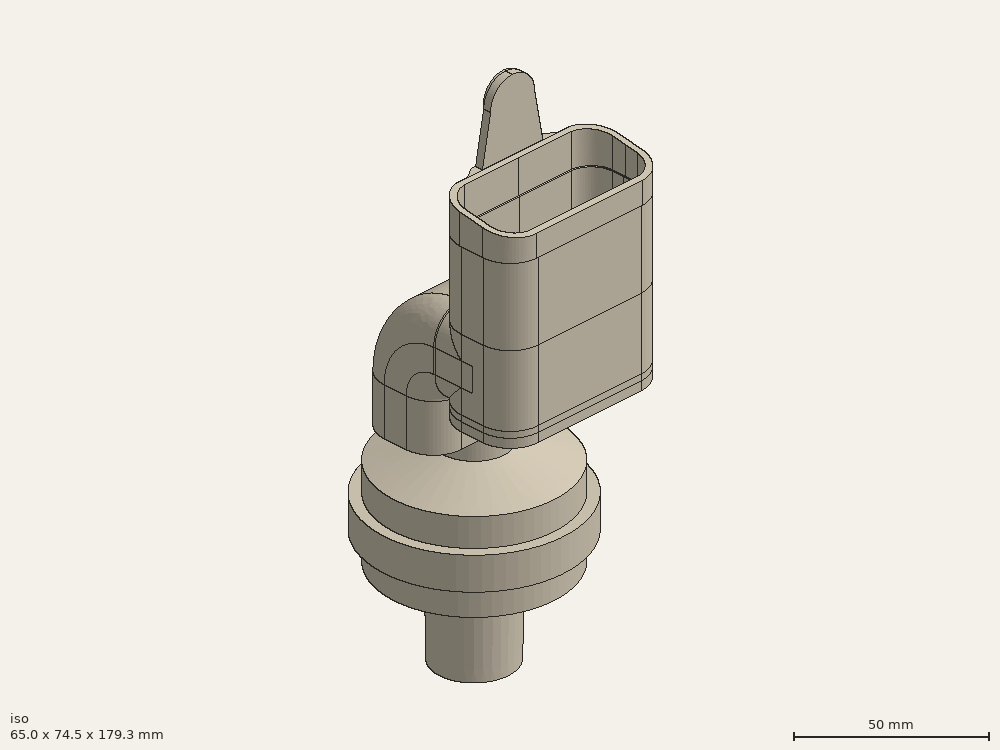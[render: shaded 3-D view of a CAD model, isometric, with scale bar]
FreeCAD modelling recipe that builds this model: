
FCSTD DOCUMENT  (FreeCAD 0.18R4 (GitTag))
Label: decathlon_easy_breath_adaptor_v2
License: All rights reserved
LicenseURL: http://en.wikipedia.org/wiki/All_rights_reserved
objects: Sketcher::SketchObject×18, PartDesign::Body×14, PartDesign::Pad×13, Part::Cut×5, Part::MultiFuse×5, PartDesign::Revolution×2, Part::Mirroring×1, Mesh::Feature×1
note: 73 computed .brp shape members not serialized (recipe doc carries the construction recipe); baked Part::Feature solids carry a one-line shape summary decoded from their .brp

FEATURE [Sketcher::SketchObject] Sketch001
  MapMode = 5
  Support = -> [XY_Plane001]
  sketch-geometry (24):
    g0: ArcOfCircle CenterX=18.75 CenterY=4 CenterZ=0 NormalX=0 NormalY=0 NormalZ=1 AngleXU=0 Radius=7.5 StartAngle=0 EndAngle=1.5708
    g1: LineSegment StartX=0 StartY=11.5 StartZ=0 EndX=18.75 EndY=11.5 EndZ=0
    g2: LineSegment StartX=26.25 StartY=4 StartZ=0 EndX=26.25 EndY=1.14244e-07 EndZ=0
    g3: LineSegment StartX=0 StartY=11.5 StartZ=0 EndX=-18.75 EndY=11.5 EndZ=0
    g4: ArcOfCircle CenterX=-18.75 CenterY=4 CenterZ=0 NormalX=0 NormalY=0 NormalZ=1 AngleXU=0 Radius=7.5 StartAngle=1.5708 EndAngle=3.14159
    g5: LineSegment StartX=-26.25 StartY=4 StartZ=0 EndX=-26.25 EndY=0 EndZ=0
    g6: LineSegment StartX=-26.25 StartY=0 StartZ=0 EndX=-26.25 EndY=-4 EndZ=0
    g7: ArcOfCircle CenterX=-18.75 CenterY=-4 CenterZ=0 NormalX=0 NormalY=0 NormalZ=1 AngleXU=0 Radius=7.5 StartAngle=3.14159 EndAngle=4.71239
    g8: ArcOfCircle CenterX=18.75 CenterY=-4 CenterZ=0 NormalX=0 NormalY=0 NormalZ=1 AngleXU=0 Radius=7.5 StartAngle=4.71239 EndAngle=6.28319
    g9: LineSegment StartX=26.25 StartY=-4 StartZ=0 EndX=26.25 EndY=1.14244e-07 EndZ=0
    g10: LineSegment StartX=-18.75 StartY=-11.5 StartZ=0 EndX=0 EndY=-11.5 EndZ=0
    g11: LineSegment StartX=0 StartY=-11.5 StartZ=0 EndX=18.75 EndY=-11.5 EndZ=0
    g12: LineSegment StartX=-18.75 StartY=-14 StartZ=0 EndX=18.75 EndY=-14 EndZ=0
    g13: ArcOfCircle CenterX=-18.75 CenterY=-4 CenterZ=0 NormalX=0 NormalY=0 NormalZ=1 AngleXU=0 Radius=10 StartAngle=3.14159 EndAngle=4.71239
    g14: LineSegment StartX=-28.75 StartY=-4 StartZ=0 EndX=-28.75 EndY=4 EndZ=0
    g15: ArcOfCircle CenterX=-18.75 CenterY=4 CenterZ=0 NormalX=0 NormalY=0 NormalZ=1 AngleXU=0 Radius=10 StartAngle=1.5708 EndAngle=3.14159
    g16: LineSegment StartX=-18.75 StartY=14 StartZ=0 EndX=-16.75 EndY=14 EndZ=0
    g17: LineSegment StartX=16.75 StartY=14 StartZ=0 EndX=18.75 EndY=14 EndZ=0
    g18: ArcOfCircle CenterX=18.75 CenterY=4 CenterZ=0 NormalX=0 NormalY=0 NormalZ=1 AngleXU=0 Radius=10 StartAngle=0 EndAngle=1.5708
    g19: ArcOfCircle CenterX=18.75 CenterY=-4 CenterZ=0 NormalX=0 NormalY=0 NormalZ=1 AngleXU=0 Radius=10 StartAngle=4.71239 EndAngle=6.28319
    g20: LineSegment StartX=28.75 StartY=4 StartZ=0 EndX=28.75 EndY=-4 EndZ=0
    g21: LineSegment StartX=-16.75 StartY=14 StartZ=0 EndX=-12.5 EndY=16.5 EndZ=0
    g22: LineSegment StartX=-12.5 StartY=16.5 StartZ=0 EndX=12.5 EndY=16.5 EndZ=0
    g23: LineSegment StartX=12.5 StartY=16.5 StartZ=0 EndX=16.75 EndY=14 EndZ=0
  constraints (71):
    c: PointOnObject(g1,g-2)
    c: Coincident(g1,g0)
    c: Horizontal(g1)
    c: Coincident(g2,g0)
    c: Vertical(g2)
    c: Coincident(g3,g1)
    c: Horizontal(g3)
    c: Coincident(g4,g3)
    c: Coincident(g5,g4)
    c: PointOnObject(g5,g-1)
    c: Vertical(g5)
    c: Coincident(g6,g5)
    c: Vertical(g6)
    c: Coincident(g7,g6)
    c: Coincident(g9,g8)
    c: Coincident(g9,g2)
    c: Vertical(g9)
    c: Coincident(g10,g7)
    c: PointOnObject(g10,g-2)
    c: Horizontal(g10)
    c: Coincident(g11,g10)
    c: Coincident(g8,g11)
    c: Equal(g3,g1)
    c: Equal(g1,g10)
    c: Equal(g10,g11)
    c: Equal(g9,g2)
    c: Equal(g2,g5)
    c: Equal(g5,g6)
    c: DistanceY(g10,g1) = 23
    c: DistanceX(g5,g2) = 52.5
    c: Symmetric(g4,g7,g-1)
    c: Symmetric(g0,g8,g-1)
    c: Symmetric(g4,g0,g-2)
    c: DistanceY(g8,g0) = 8
    c: Radius(g0) = 7.5
    c: Horizontal(g0,g0)
    c: Horizontal(g11)
    c: Horizontal(g12)
    c: Vertical(g7,g12)
    c: Coincident(g13,g7)
    c: Coincident(g13,g12)
    c: Coincident(g14,g13)
    c: Vertical(g14)
    c: Coincident(g15,g4)
    c: Coincident(g15,g14)
    c: Coincident(g16,g15)
    c: Coincident(g18,g0)
    c: Coincident(g18,g17)
    c: Vertical(g12,g8)
    c: Coincident(g19,g8)
    c: Coincident(g19,g12)
    c: Coincident(g20,g18)
    c: Coincident(g20,g19)
    c: DistanceY(g12,g7) = 2.5
    c: Horizontal(g6,g13)
    c: Horizontal(g14,g4)
    c: Vertical(g18,g19)
    c: Horizontal(g0,g18)
    c: Vertical(g17,g0)
    c: Coincident(g16,g21)
    c: Coincident(g21,g22)
    c: Coincident(g22,g23)
    c: Coincident(g23,g17)
    c: Horizontal(g16)
    c: Equal(g17,g16)
    c: Symmetric(g16,g17,g-2)
    c: DistanceY(g1,g21) = 5
    c: Symmetric(g22,g21,g-2)
    c: Horizontal(g19,g8)
    c: DistanceX(g21,g22) = 25
    c: DistanceX(g15,g16) = 2
FEATURE [Sketcher::SketchObject] Sketch002
  MapMode = 5
  Support = -> [XY_Plane002]
  sketch-geometry (26):
    g0: ArcOfCircle CenterX=18.75 CenterY=4 CenterZ=0 NormalX=0 NormalY=0 NormalZ=1 AngleXU=0 Radius=7.5 StartAngle=0 EndAngle=1.57079
    g1: LineSegment StartX=26.25 StartY=4 StartZ=0 EndX=26.25 EndY=0 EndZ=0
    g2: ArcOfCircle CenterX=-18.75 CenterY=4 CenterZ=0 NormalX=0 NormalY=0 NormalZ=1 AngleXU=0 Radius=7.5 StartAngle=1.5708 EndAngle=3.14159
    g3: LineSegment StartX=-26.25 StartY=4 StartZ=0 EndX=-26.25 EndY=0 EndZ=0
    g4: LineSegment StartX=-26.25 StartY=0 StartZ=0 EndX=-26.25 EndY=-4 EndZ=0
    g5: ArcOfCircle CenterX=-18.75 CenterY=-4 CenterZ=0 NormalX=0 NormalY=0 NormalZ=1 AngleXU=0 Radius=7.5 StartAngle=3.14159 EndAngle=4.71239
    g6: ArcOfCircle CenterX=18.75 CenterY=-4 CenterZ=0 NormalX=0 NormalY=0 NormalZ=1 AngleXU=0 Radius=7.5 StartAngle=4.71239 EndAngle=6.28319
    g7: LineSegment StartX=26.25 StartY=-4 StartZ=0 EndX=26.25 EndY=0 EndZ=0
    g8: LineSegment StartX=-18.75 StartY=-14 StartZ=0 EndX=18.75 EndY=-14 EndZ=0
    g9: ArcOfCircle CenterX=-18.75 CenterY=-4 CenterZ=0 NormalX=0 NormalY=0 NormalZ=1 AngleXU=0 Radius=10 StartAngle=3.14159 EndAngle=4.71239
    g10: LineSegment StartX=-28.75 StartY=-4 StartZ=0 EndX=-28.75 EndY=4 EndZ=0
    g11: ArcOfCircle CenterX=-18.75 CenterY=4 CenterZ=0 NormalX=0 NormalY=0 NormalZ=1 AngleXU=0 Radius=10 StartAngle=1.5708 EndAngle=3.14159
    g12: LineSegment StartX=-18.75 StartY=14 StartZ=0 EndX=18.75 EndY=14 EndZ=0
    g13: ArcOfCircle CenterX=18.75 CenterY=4 CenterZ=0 NormalX=0 NormalY=0 NormalZ=1 AngleXU=0 Radius=10 StartAngle=0 EndAngle=1.5708
    g14: ArcOfCircle CenterX=18.75 CenterY=-4 CenterZ=0 NormalX=0 NormalY=0 NormalZ=1 AngleXU=0 Radius=10 StartAngle=4.71239 EndAngle=6.28319
    g15: LineSegment StartX=28.75 StartY=4 StartZ=0 EndX=28.75 EndY=-4 EndZ=0
    g16: LineSegment StartX=-18.75 StartY=11.5 StartZ=0 EndX=-13.75 EndY=11.5 EndZ=0
    g17: LineSegment StartX=-13.75 StartY=11.5 StartZ=0 EndX=-13.75 EndY=-11.5 EndZ=0
    g18: LineSegment StartX=-13.75 StartY=-11.5 StartZ=0 EndX=-18.75 EndY=-11.5 EndZ=0
    g19: LineSegment StartX=-11.75 StartY=-11.5 StartZ=0 EndX=-11.75 EndY=11.5 EndZ=0
    g20: LineSegment StartX=-11.75 StartY=11.5 StartZ=0 EndX=11.75 EndY=11.5 EndZ=0
    g21: LineSegment StartX=11.75 StartY=11.5 StartZ=0 EndX=11.75 EndY=-11.5 EndZ=0
    g22: LineSegment StartX=11.75 StartY=-11.5 StartZ=0 EndX=-11.75 EndY=-11.5 EndZ=0
    g23: LineSegment StartX=18.75 StartY=-11.5 StartZ=0 EndX=13.75 EndY=-11.5 EndZ=0
    g24: LineSegment StartX=13.75 StartY=-11.5 StartZ=0 EndX=13.75 EndY=11.5 EndZ=0
    g25: LineSegment StartX=13.75 StartY=11.5 StartZ=0 EndX=18.75 EndY=11.5 EndZ=0
  constraints (75):
    c: Coincident(g1,g0)
    c: Vertical(g1)
    c: Coincident(g3,g2)
    c: PointOnObject(g3,g-1)
    c: Vertical(g3)
    c: Coincident(g4,g3)
    c: Vertical(g4)
    c: Coincident(g5,g4)
    c: Coincident(g7,g6)
    c: Coincident(g7,g1)
    c: Vertical(g7)
    c: Equal(g7,g1)
    c: Equal(g1,g3)
    c: Equal(g3,g4)
    c: DistanceX(g3,g1) = 52.5
    c: Symmetric(g2,g5,g-1)
    c: Symmetric(g0,g6,g-1)
    c: Symmetric(g2,g0,g-2)
    c: DistanceY(g6,g0) = 8
    c: Radius(g0) = 7.5
    c: Horizontal(g0,g0)
    c: Horizontal(g8)
    c: Vertical(g5,g8)
    c: Coincident(g9,g5)
    c: Coincident(g9,g8)
    c: Coincident(g10,g9)
    c: Vertical(g10)
    c: Coincident(g11,g2)
    c: Coincident(g11,g10)
    c: Coincident(g12,g11)
    c: Coincident(g13,g0)
    c: Vertical(g8,g6)
    c: Coincident(g14,g6)
    c: Coincident(g14,g8)
    c: Coincident(g15,g13)
    c: Coincident(g15,g14)
    c: DistanceY(g8,g5) = 2.5
    c: Horizontal(g4,g9)
    c: Horizontal(g10,g2)
    c: Vertical(g13,g14)
    c: Horizontal(g0,g13)
    c: Vertical(g13,g0)
    c: Horizontal(g12)
    c: Horizontal(g14,g6)
    c: Coincident(g16,g2)
    c: Horizontal(g16)
    c: Coincident(g16,g17)
    c: Vertical(g17)
    c: Coincident(g17,g18)
    c: Coincident(g18,g5)
    c: Vertical(g19)
    c: Coincident(g19,g20)
    c: Coincident(g20,g21)
    c: Coincident(g21,g22)
    c: Coincident(g22,g19)
    c: Tangent(g6,g23) = 1.5708
    c: Coincident(g23,g24)
    c: Vertical(g24)
    c: Coincident(g24,g25)
    c: Coincident(g25,g0)
    c: DistanceX(g19,g20) = 23.5
    c: DistanceX(g16,g19) = 2
    c: Symmetric(g24,g16,g-2)
    c: Symmetric(g20,g19,g-2)
    c: Equal(g17,g19)
    c: Equal(g19,g21)
    c: Equal(g21,g24)
    c: Horizontal(g20,g24)
    c: Coincident(g12,g13)
    c: Equal(g20,g22)
    c: Equal(g22,g20)
    c: Vertical(g2,g11)
    c: Vertical(g2,g5)
    c: Symmetric(g2,g0,g-2)
    c: Symmetric(g2,g0,g-2)
FEATURE [PartDesign::Pad] Pad002
  Length = 26
  Length2 = 100
  Profile = -> Sketch002
  Reversed = true
  Type = 0
FEATURE [PartDesign::Body] Body002
  Group = -> [Sketch002,Pad002]
  Origin = -> Origin002
  Placement = pos=(0,0,-22) rot=(0,0,1;0rad)
  Tip = -> Pad002
FEATURE [Sketcher::SketchObject] Sketch006
  MapMode = 5
  Support = -> [XY_Plane006]
  sketch-geometry (9):
    g0: LineSegment StartX=-18.75 StartY=-14 StartZ=0 EndX=18.75 EndY=-14 EndZ=0
    g1: ArcOfCircle CenterX=-18.75 CenterY=-4 CenterZ=0 NormalX=0 NormalY=0 NormalZ=1 AngleXU=0 Radius=10 StartAngle=3.14159 EndAngle=4.71239
    g2: LineSegment StartX=-28.75 StartY=-4 StartZ=0 EndX=-28.75 EndY=4 EndZ=0
    g3: ArcOfCircle CenterX=-18.75 CenterY=4 CenterZ=0 NormalX=0 NormalY=0 NormalZ=1 AngleXU=0 Radius=10 StartAngle=1.5708 EndAngle=3.14159
    g4: LineSegment StartX=-18.75 StartY=14 StartZ=0 EndX=18.75 EndY=14 EndZ=0
    g5: ArcOfCircle CenterX=18.75 CenterY=4 CenterZ=0 NormalX=0 NormalY=0 NormalZ=1 AngleXU=0 Radius=10 StartAngle=0 EndAngle=1.5708
    g6: ArcOfCircle CenterX=18.75 CenterY=-4 CenterZ=0 NormalX=0 NormalY=0 NormalZ=1 AngleXU=0 Radius=10 StartAngle=4.71239 EndAngle=6.28319
    g7: LineSegment StartX=28.75 StartY=4 StartZ=0 EndX=28.75 EndY=-4 EndZ=0
    g8: Circle CenterX=0 CenterY=0 CenterZ=0 NormalX=0 NormalY=0 NormalZ=1 AngleXU=0 Radius=11.5009
  constraints (13):
    c: Horizontal(g0)
    c: Coincident(g1,g0)
    c: Coincident(g2,g1)
    c: Vertical(g2)
    c: Coincident(g3,g2)
    c: Coincident(g4,g3)
    c: Coincident(g6,g0)
    c: Coincident(g7,g5)
    c: Coincident(g7,g6)
    c: Vertical(g5,g6)
    c: Horizontal(g4)
    c: Coincident(g4,g5)
    c: Coincident(g8,g-1)
FEATURE [PartDesign::Pad] Pad003
  Length = 16
  Length2 = 100
  Profile = -> Sketch006
  Reversed = true
  Type = 0
FEATURE [PartDesign::Body] Body006  label="lid-out"
  Group = -> [Sketch006,Pad003]
  Origin = -> Origin006
  Placement = pos=(0,28,-48) rot=(1,0,0;0rad)
  Tip = -> Pad003
FEATURE [Sketcher::SketchObject] Sketch008
  MapMode = 5
  Support = -> [XY_Plane008]
  sketch-geometry (9):
    g0: LineSegment StartX=-18.75 StartY=-14 StartZ=0 EndX=18.75 EndY=-14 EndZ=0
    g1: ArcOfCircle CenterX=-18.75 CenterY=-4 CenterZ=0 NormalX=0 NormalY=0 NormalZ=1 AngleXU=0 Radius=10 StartAngle=3.14159 EndAngle=4.71239
    g2: LineSegment StartX=-28.75 StartY=-4 StartZ=0 EndX=-28.75 EndY=4 EndZ=0
    g3: ArcOfCircle CenterX=-18.75 CenterY=4 CenterZ=0 NormalX=0 NormalY=0 NormalZ=1 AngleXU=0 Radius=10 StartAngle=1.5708 EndAngle=3.14159
    g4: LineSegment StartX=-18.75 StartY=14 StartZ=0 EndX=18.75 EndY=14 EndZ=0
    g5: ArcOfCircle CenterX=18.75 CenterY=4 CenterZ=0 NormalX=0 NormalY=0 NormalZ=1 AngleXU=0 Radius=10 StartAngle=0 EndAngle=1.5708
    g6: ArcOfCircle CenterX=18.75 CenterY=-4 CenterZ=0 NormalX=0 NormalY=0 NormalZ=1 AngleXU=0 Radius=10 StartAngle=4.71239 EndAngle=6.28319
    g7: LineSegment StartX=28.75 StartY=4 StartZ=0 EndX=28.75 EndY=-4 EndZ=0
    g8: Circle CenterX=0 CenterY=0 CenterZ=0 NormalX=0 NormalY=0 NormalZ=1 AngleXU=0 Radius=11.5009
  constraints (13):
    c: Horizontal(g0)
    c: Coincident(g1,g0)
    c: Coincident(g2,g1)
    c: Vertical(g2)
    c: Coincident(g3,g2)
    c: Coincident(g4,g3)
    c: Coincident(g6,g0)
    c: Coincident(g7,g5)
    c: Coincident(g7,g6)
    c: Vertical(g5,g6)
    c: Horizontal(g4)
    c: Coincident(g4,g5)
    c: Coincident(g8,g-1)
FEATURE [PartDesign::Pad] Pad005
  Length = 5
  Length2 = 100
  Profile = -> Sketch008
  Reversed = true
  Type = 0
FEATURE [PartDesign::Body] Body008  label="lid-in"
  Group = -> [Sketch008,Pad005]
  Origin = -> Origin008
  Placement = pos=(0,0,-46) rot=(0,0,1;0rad)
  Tip = -> Pad005
FEATURE [Sketcher::SketchObject] Sketch009
  MapMode = 5
  Support = -> [XY_Plane009]
  sketch-geometry (1):
    g0: Circle CenterX=0 CenterY=0 CenterZ=0 NormalX=0 NormalY=0 NormalZ=1 AngleXU=0 Radius=11.5
  constraints (1):
    c: Radius(g0) = 11.5
FEATURE [PartDesign::Pad] Pad006
  Length = 50
  Length2 = 100
  Profile = -> Sketch009
  Reversed = true
  Type = 0
FEATURE [Sketcher::SketchObject] Sketch010
  MapMode = 5
  Support = -> [XY_Plane010]
  sketch-geometry (12):
    g0: ArcOfCircle CenterX=18.75 CenterY=4 CenterZ=0 NormalX=0 NormalY=0 NormalZ=1 AngleXU=0 Radius=7.5 StartAngle=0 EndAngle=1.5708
    g1: LineSegment StartX=0 StartY=11.5 StartZ=0 EndX=18.75 EndY=11.5 EndZ=0
    g2: LineSegment StartX=26.25 StartY=4 StartZ=0 EndX=26.25 EndY=1.14244e-07 EndZ=0
    g3: LineSegment StartX=0 StartY=11.5 StartZ=0 EndX=-18.75 EndY=11.5 EndZ=0
    g4: ArcOfCircle CenterX=-18.75 CenterY=4 CenterZ=0 NormalX=0 NormalY=0 NormalZ=1 AngleXU=0 Radius=7.5 StartAngle=1.5708 EndAngle=3.14159
    g5: LineSegment StartX=-26.25 StartY=4 StartZ=0 EndX=-26.25 EndY=0 EndZ=0
    g6: LineSegment StartX=-26.25 StartY=0 StartZ=0 EndX=-26.25 EndY=-4 EndZ=0
    g7: ArcOfCircle CenterX=-18.75 CenterY=-4 CenterZ=0 NormalX=0 NormalY=0 NormalZ=1 AngleXU=0 Radius=7.5 StartAngle=3.14159 EndAngle=4.71239
    g8: ArcOfCircle CenterX=18.75 CenterY=-4 CenterZ=0 NormalX=0 NormalY=0 NormalZ=1 AngleXU=0 Radius=7.5 StartAngle=4.71239 EndAngle=6.28319
    g9: LineSegment StartX=26.25 StartY=-4 StartZ=0 EndX=26.25 EndY=1.14244e-07 EndZ=0
    g10: LineSegment StartX=-18.75 StartY=-11.5 StartZ=0 EndX=0 EndY=-11.5 EndZ=0
    g11: LineSegment StartX=0 StartY=-11.5 StartZ=0 EndX=18.75 EndY=-11.5 EndZ=0
  constraints (37):
    c: PointOnObject(g1,g-2)
    c: Coincident(g1,g0)
    c: Horizontal(g1)
    c: Coincident(g2,g0)
    c: Vertical(g2)
    c: Coincident(g3,g1)
    c: Horizontal(g3)
    c: Coincident(g4,g3)
    c: Coincident(g5,g4)
    c: PointOnObject(g5,g-1)
    c: Vertical(g5)
    c: Coincident(g6,g5)
    c: Vertical(g6)
    c: Coincident(g7,g6)
    c: Coincident(g9,g8)
    c: Coincident(g9,g2)
    c: Vertical(g9)
    c: Coincident(g10,g7)
    c: PointOnObject(g10,g-2)
    c: Horizontal(g10)
    c: Coincident(g11,g10)
    c: Coincident(g8,g11)
    c: Equal(g3,g1)
    c: Equal(g1,g10)
    c: Equal(g10,g11)
    c: Equal(g9,g2)
    c: Equal(g2,g5)
    c: Equal(g5,g6)
    c: DistanceY(g10,g1) = 23
    c: DistanceX(g5,g2) = 52.5
    c: Symmetric(g4,g7,g-1)
    c: Symmetric(g0,g8,g-1)
    c: Symmetric(g4,g0,g-2)
    c: DistanceY(g8,g0) = 8
    c: Radius(g0) = 7.5
    c: Horizontal(g0,g0)
    c: Horizontal(g11)
FEATURE [PartDesign::Pad] Pad007
  Length = 34
  Length2 = 100
  Profile = -> Sketch010
  Reversed = true
  Type = 0
FEATURE [PartDesign::Body] Body010
  Group = -> [Sketch010,Pad007]
  Origin = -> Origin010
  Tip = -> Pad007
FEATURE [Sketcher::SketchObject] Sketch011
  MapMode = 5
  Support = -> [XY_Plane011]
  sketch-geometry (8):
    g0: ArcOfCircle CenterX=18.75 CenterY=4 CenterZ=0 NormalX=0 NormalY=0 NormalZ=1 AngleXU=0 Radius=7.5 StartAngle=0 EndAngle=1.57079
    g1: LineSegment StartX=26.25 StartY=4 StartZ=0 EndX=26.25 EndY=0 EndZ=0
    g2: ArcOfCircle CenterX=18.75 CenterY=-4 CenterZ=0 NormalX=0 NormalY=0 NormalZ=1 AngleXU=0 Radius=7.5 StartAngle=4.71239 EndAngle=6.28319
    g3: LineSegment StartX=26.25 StartY=-4 StartZ=0 EndX=26.25 EndY=0 EndZ=0
    g4: LineSegment StartX=28.75 StartY=4 StartZ=0 EndX=28.75 EndY=-4 EndZ=0
    g5: LineSegment StartX=18.75 StartY=-11.5 StartZ=0 EndX=13.75 EndY=-11.5 EndZ=0
    g6: LineSegment StartX=13.75 StartY=-11.5 StartZ=0 EndX=13.75 EndY=11.5 EndZ=0
    g7: LineSegment StartX=13.75 StartY=11.5 StartZ=0 EndX=18.75 EndY=11.5 EndZ=0
  constraints (18):
    c: Coincident(g1,g0)
    c: Vertical(g1)
    c: Coincident(g3,g2)
    c: Coincident(g3,g1)
    c: Vertical(g3)
    c: Equal(g3,g1)
    c: Symmetric(g0,g2,g-1)
    c: DistanceY(g2,g0) = 8
    c: Radius(g0) = 7.5
    c: Horizontal(g0,g0)
    c: Vertical(g4,g4)
    c: Horizontal(g0,g4)
    c: Horizontal(g4,g2)
    c: Tangent(g2,g5) = 1.5708
    c: Coincident(g5,g6)
    c: Vertical(g6)
    c: Coincident(g6,g7)
    c: Coincident(g7,g0)
FEATURE [PartDesign::Pad] Pad008
  Length = 15
  Length2 = 100
  Profile = -> Sketch011
  Reversed = true
  Type = 0
FEATURE [PartDesign::Body] Body011
  Group = -> [Sketch011,Pad008]
  Origin = -> Origin011
  Placement = pos=(0,0,-34) rot=(1,0,0;1.5708rad)
  Tip = -> Pad008
FEATURE [Sketcher::SketchObject] Sketch012
  MapMode = 5
  Support = -> [XY_Plane012]
  sketch-geometry (8):
    g0: ArcOfCircle CenterX=18.75 CenterY=4 CenterZ=0 NormalX=0 NormalY=0 NormalZ=1 AngleXU=0 Radius=7.5 StartAngle=0 EndAngle=1.57079
    g1: LineSegment StartX=26.25 StartY=4 StartZ=0 EndX=26.25 EndY=0 EndZ=0
    g2: ArcOfCircle CenterX=18.75 CenterY=-4 CenterZ=0 NormalX=0 NormalY=0 NormalZ=1 AngleXU=0 Radius=7.5 StartAngle=4.71239 EndAngle=6.28319
    g3: LineSegment StartX=26.25 StartY=-4 StartZ=0 EndX=26.25 EndY=0 EndZ=0
    g4: LineSegment StartX=28.75 StartY=4 StartZ=0 EndX=28.75 EndY=-4 EndZ=0
    g5: LineSegment StartX=18.75 StartY=-11.5 StartZ=0 EndX=13.75 EndY=-11.5 EndZ=0
    g6: LineSegment StartX=13.75 StartY=-11.5 StartZ=0 EndX=13.75 EndY=11.5 EndZ=0
    g7: LineSegment StartX=13.75 StartY=11.5 StartZ=0 EndX=18.75 EndY=11.5 EndZ=0
  constraints (18):
    c: Coincident(g1,g0)
    c: Vertical(g1)
    c: Coincident(g3,g2)
    c: Coincident(g3,g1)
    c: Vertical(g3)
    c: Equal(g3,g1)
    c: Symmetric(g0,g2,g-1)
    c: DistanceY(g2,g0) = 8
    c: Radius(g0) = 7.5
    c: Horizontal(g0,g0)
    c: Vertical(g4,g4)
    c: Horizontal(g0,g4)
    c: Horizontal(g4,g2)
    c: Tangent(g2,g5) = 1.5708
    c: Coincident(g5,g6)
    c: Vertical(g6)
    c: Coincident(g6,g7)
    c: Coincident(g7,g0)
FEATURE [PartDesign::Pad] Pad009
  Length = 15
  Length2 = 100
  Profile = -> Sketch012
  Reversed = true
  Type = 0
FEATURE [PartDesign::Body] Body012
  Group = -> [Sketch012,Pad009]
  Origin = -> Origin012
  Placement = pos=(0,0,-34) rot=(1,0,0;1.5708rad)
  Tip = -> Pad009
FEATURE [Part::Mirroring] Part__Mirroring  label="Body012 (Mirror #1)"
  Base = (0,0,0)
  Normal = (1,0,0)
  Source = -> Body012
FEATURE [Part::Cut] Cut002
  Base = -> Body002
  Tool = -> Body011
FEATURE [Part::Cut] Cut003  label="transition-in"
  Base = -> Cut002
  Tool = -> Part__Mirroring
FEATURE [Sketcher::SketchObject] Sketch013
  MapMode = 5
  Support = -> [XY_Plane013]
  sketch-geometry (24):
    g0: ArcOfCircle CenterX=19.0026 CenterY=4.25 CenterZ=0 NormalX=0 NormalY=0 NormalZ=1 AngleXU=0 Radius=7.75 StartAngle=0 EndAngle=1.51871
    g1: LineSegment StartX=0 StartY=11.9895 StartZ=0 EndX=19.4062 EndY=11.9895 EndZ=0
    g2: LineSegment StartX=26.7526 StartY=4.25 StartZ=0 EndX=26.7526 EndY=-0.28543 EndZ=0
    g3: LineSegment StartX=0 StartY=11.9895 StartZ=0 EndX=-19.4062 EndY=11.9895 EndZ=0
    g4: ArcOfCircle CenterX=-19.0026 CenterY=4.25 CenterZ=0 NormalX=0 NormalY=0 NormalZ=1 AngleXU=0 Radius=7.75 StartAngle=1.62289 EndAngle=3.10475
    g5: LineSegment StartX=-26.7474 StartY=4.53543 StartZ=0 EndX=-26.7474 EndY=0 EndZ=0
    g6: LineSegment StartX=-26.7474 StartY=0 StartZ=0 EndX=-26.7474 EndY=-3.61176 EndZ=0
    g7: ArcOfCircle CenterX=-19.0026 CenterY=-4.25 CenterZ=0 NormalX=0 NormalY=0 NormalZ=1 AngleXU=0 Radius=7.771 StartAngle=3.05937 EndAngle=4.66044
    g8: ArcOfCircle CenterX=19.0026 CenterY=-4.25 CenterZ=0 NormalX=0 NormalY=0 NormalZ=1 AngleXU=0 Radius=7.771 StartAngle=4.76434 EndAngle=6.20966
    g9: LineSegment StartX=26.7526 StartY=-4.82086 StartZ=0 EndX=26.7526 EndY=-0.28543 EndZ=0
    g10: LineSegment StartX=-19.4062 StartY=-12.0105 StartZ=0 EndX=0 EndY=-12.0105 EndZ=0
    g11: LineSegment StartX=0 StartY=-12.0105 StartZ=0 EndX=19.4062 EndY=-12.0105 EndZ=0
    g12: LineSegment StartX=-19.4062 StartY=-14.0105 StartZ=0 EndX=19.4062 EndY=-14.0105 EndZ=0
    g13: ArcOfCircle CenterX=-19.0026 CenterY=-4.25 CenterZ=0 NormalX=0 NormalY=0 NormalZ=1 AngleXU=0 Radius=9.76885 StartAngle=3.07621 EndAngle=4.67107
    g14: LineSegment StartX=-28.7506 StartY=-3.61176 StartZ=0 EndX=-28.7506 EndY=4.53543 EndZ=0
    g15: ArcOfCircle CenterX=-19.0026 CenterY=4.25 CenterZ=0 NormalX=0 NormalY=0 NormalZ=1 AngleXU=0 Radius=9.75216 StartAngle=1.61219 EndAngle=3.11232
    g16: LineSegment StartX=-19.4062 StartY=13.9938 StartZ=0 EndX=-16.4062 EndY=13.9938 EndZ=0
    g17: LineSegment StartX=16.4062 StartY=13.9938 StartZ=0 EndX=19.4062 EndY=13.9938 EndZ=0
    g18: ArcOfCircle CenterX=19.0026 CenterY=4.25 CenterZ=0 NormalX=0 NormalY=0 NormalZ=1 AngleXU=0 Radius=9.75216 StartAngle=0 EndAngle=1.52941
    g19: ArcOfCircle CenterX=19.0026 CenterY=-4.25 CenterZ=0 NormalX=0 NormalY=0 NormalZ=1 AngleXU=0 Radius=9.76885 StartAngle=4.75371 EndAngle=6.22472
    g20: LineSegment StartX=28.7548 StartY=4.25 StartZ=0 EndX=28.7548 EndY=-4.82086 EndZ=0
    g21: LineSegment StartX=-16.4062 StartY=13.9938 StartZ=0 EndX=-12.5 EndY=16.4895 EndZ=0
    g22: LineSegment StartX=-12.5 StartY=16.4895 StartZ=0 EndX=12.5 EndY=16.4895 EndZ=0
    g23: LineSegment StartX=12.5 StartY=16.4895 StartZ=0 EndX=16.4062 EndY=13.9938 EndZ=0
  constraints (70):
    c: PointOnObject(g1,g-2)
    c: Coincident(g1,g0)
    c: Horizontal(g1)
    c: Coincident(g2,g0)
    c: Vertical(g2)
    c: Coincident(g3,g1)
    c: Horizontal(g3)
    c: Coincident(g4,g3)
    c: Coincident(g5,g4)
    c: PointOnObject(g5,g-1)
    c: Vertical(g5)
    c: Coincident(g6,g5)
    c: Vertical(g6)
    c: Coincident(g7,g6)
    c: Coincident(g9,g8)
    c: Coincident(g9,g2)
    c: Vertical(g9)
    c: Coincident(g10,g7)
    c: PointOnObject(g10,g-2)
    c: Horizontal(g10)
    c: Coincident(g11,g10)
    c: Coincident(g8,g11)
    c: Equal(g3,g1)
    c: Equal(g1,g10)
    c: Equal(g10,g11)
    c: Equal(g9,g2)
    c: Equal(g2,g5)
    c: DistanceY(g10,g1) = 24
    c: DistanceX(g5,g2) = 53.5
    c: Symmetric(g4,g7,g-1)
    c: Symmetric(g0,g8,g-1)
    c: Symmetric(g4,g0,g-2)
    c: DistanceY(g8,g0) = 8.5
    c: Radius(g0) = 7.75
    c: Horizontal(g0,g0)
    c: Horizontal(g11)
    c: Horizontal(g12)
    c: Vertical(g7,g12)
    c: Coincident(g13,g7)
    c: Coincident(g13,g12)
    c: Coincident(g14,g13)
    c: Vertical(g14)
    c: Coincident(g15,g4)
    c: Coincident(g15,g14)
    c: Coincident(g16,g15)
    c: Coincident(g18,g0)
    c: Coincident(g18,g17)
    c: Vertical(g12,g8)
    c: Coincident(g19,g8)
    c: Coincident(g19,g12)
    c: Coincident(g20,g18)
    c: Coincident(g20,g19)
    c: DistanceY(g12,g7) = 2
    c: Horizontal(g6,g13)
    c: Horizontal(g14,g4)
    c: Vertical(g18,g19)
    c: Horizontal(g0,g18)
    c: Vertical(g17,g0)
    c: Coincident(g16,g21)
    c: Coincident(g21,g22)
    c: Coincident(g22,g23)
    c: Coincident(g23,g17)
    c: Horizontal(g16)
    c: Equal(g17,g16)
    c: Symmetric(g16,g17,g-2)
    c: DistanceY(g1,g21) = 4.5
    c: Symmetric(g22,g21,g-2)
    c: Horizontal(g19,g8)
    c: DistanceX(g21,g22) = 25
    c: DistanceX(g15,g16) = 3
FEATURE [PartDesign::Pad] Pad010
  Length = 11.5
  Length2 = 100
  Profile = -> Sketch013
  Type = 0
FEATURE [PartDesign::Body] Body013
  Group = -> [Sketch013,Pad010]
  Origin = -> Origin013
  Placement = pos=(0,0,11) rot=(0,0,1;0rad)
  Tip = -> Pad010
FEATURE [Sketcher::SketchObject] Sketch014
  MapMode = 5
  Support = -> [XY_Plane014]
  sketch-geometry (4):
    g0: LineSegment StartX=-42.12 StartY=29 StartZ=0 EndX=44.5 EndY=29 EndZ=0
    g1: LineSegment StartX=44.5 StartY=29 StartZ=0 EndX=44.5 EndY=-27.321 EndZ=0
    g2: LineSegment StartX=44.5 StartY=-27.321 StartZ=0 EndX=-42.12 EndY=-27.321 EndZ=0
    g3: LineSegment StartX=-42.12 StartY=-27.321 StartZ=0 EndX=-42.12 EndY=29 EndZ=0
  constraints (8):
    c: Coincident(g0,g1)
    c: Coincident(g1,g2)
    c: Coincident(g2,g3)
    c: Coincident(g3,g0)
    c: Horizontal(g0)
    c: Horizontal(g2)
    c: Vertical(g1)
    c: Vertical(g3)
FEATURE [PartDesign::Pad] Pad011
  Length = 50
  Length2 = 100
  Profile = -> Sketch014
  Type = 0
FEATURE [Sketcher::SketchObject] Sketch
  MapMode = 5
  Placement = pos=(0,0,0) rot=(1,0,0;1.5708rad)
  Support = -> [XZ_Plane014]
FEATURE [PartDesign::Body] Body014
  Group = -> [Sketch014,Pad011,Sketch]
  Origin = -> Origin014
  Placement = pos=(0,0,71) rot=(1,0,0;3.28995rad)
  Tip = -> Pad011
FEATURE [Part::Cut] Cut004  label="adapter"
  Base = -> Body013
  Placement = pos=(0,0,-7) rot=(0,0,1;0rad)
  Tool = -> Body014
FEATURE [Sketcher::SketchObject] Sketch015
  MapMode = 5
  Placement = pos=(0,0,0) rot=(1,0,0;1.5708rad)
  Support = -> [XZ_Plane]
  sketch-geometry (5):
    g0: LineSegment StartX=-8 StartY=16 StartZ=0 EndX=-11 EndY=0 EndZ=0
    g1: LineSegment StartX=8 StartY=16 StartZ=0 EndX=11 EndY=0 EndZ=0
    g2: LineSegment StartX=-11 StartY=0 StartZ=0 EndX=11 EndY=0 EndZ=0
    g3: ArcOfCircle CenterX=8e-16 CenterY=16 CenterZ=0 NormalX=0 NormalY=0 NormalZ=1 AngleXU=0 Radius=8 StartAngle=1.5708 EndAngle=3.14159
    g4: ArcOfCircle CenterX=8e-16 CenterY=16 CenterZ=0 NormalX=0 NormalY=0 NormalZ=1 AngleXU=0 Radius=8 StartAngle=0 EndAngle=1.5708
  constraints (14):
    c: Coincident(g2,g0)
    c: Coincident(g2,g1)
    c: DistanceX(g2,g2) = 22
    c: Coincident(g3,g0)
    c: PointOnObject(g3,g-2)
    c: Coincident(g4,g3)
    c: Coincident(g4,g3)
    c: Coincident(g4,g1)
    c: DistanceY(g-1,g3) = 24
    c: Symmetric(g1,g0,g-2)
    c: DistanceY(g0,g0) = 16
    c: Horizontal(g1,g-1)
    c: Symmetric(g0,g1,g-2)
    c: Radius(g3) = 8
FEATURE [PartDesign::Pad] Pad
  Length = 2.5
  Length2 = 100
  Placement = pos=(0,0,0) rot=(1,0,0;1.5708rad)
  Profile = -> Sketch015
  Type = 0
FEATURE [Sketcher::SketchObject] Sketch016
  MapMode = 5
  Placement = pos=(0,0,0) rot=(-1,0,0;1.5708rad)
  Support = -> [Pad]
  sketch-geometry (1):
    g0: Circle CenterX=0 CenterY=-16.5 CenterZ=0 NormalX=0 NormalY=0 NormalZ=1 AngleXU=0 Radius=7.5
  constraints (1):
    c: Radius(g0) = 7.5
FEATURE [PartDesign::Pad] Pad012
  BaseFeature = -> Pad
  Length = 0.75
  Length2 = 100
  Placement = pos=(0,0,0) rot=(1,0,0;1.5708rad)
  Profile = -> Sketch016
  Type = 0
FEATURE [PartDesign::Body] Body  label="flange"
  Group = -> [Sketch015,Pad,Sketch016,Pad012]
  Origin = -> Origin
  Placement = pos=(0,16.5,15.35) rot=(0,0,1;0rad)
  Tip = -> Pad012
FEATURE [Sketcher::SketchObject] Sketch019
  MapMode = 5
  Placement = pos=(0,0,0) rot=(1,0,0;1.5708rad)
  Support = -> [XZ_Plane009]
FEATURE [PartDesign::Body] Body009
  Group = -> [Sketch009,Pad006,Sketch019]
  Origin = -> Origin009
  Tip = -> Pad006
FEATURE [Sketcher::SketchObject] Sketch020
  MapMode = 5
  Support = -> [XY_Plane015]
  sketch-geometry (19):
    g0: ArcOfCircle CenterX=18.75 CenterY=4 CenterZ=0 NormalX=0 NormalY=0 NormalZ=1 AngleXU=0 Radius=7.5 StartAngle=0 EndAngle=1.57079
    g1: LineSegment StartX=26.25 StartY=4 StartZ=0 EndX=26.25 EndY=0 EndZ=0
    g2: ArcOfCircle CenterX=-18.75 CenterY=4 CenterZ=0 NormalX=0 NormalY=0 NormalZ=1 AngleXU=0 Radius=7.5 StartAngle=1.5708 EndAngle=3.14159
    g3: LineSegment StartX=-26.25 StartY=4 StartZ=0 EndX=-26.25 EndY=0 EndZ=0
    g4: LineSegment StartX=-26.25 StartY=0 StartZ=0 EndX=-26.25 EndY=-4 EndZ=0
    g5: ArcOfCircle CenterX=-18.75 CenterY=-4 CenterZ=0 NormalX=0 NormalY=0 NormalZ=1 AngleXU=0 Radius=7.5 StartAngle=3.14159 EndAngle=4.71239
    g6: ArcOfCircle CenterX=18.75 CenterY=-4 CenterZ=0 NormalX=0 NormalY=0 NormalZ=1 AngleXU=0 Radius=7.5 StartAngle=4.71239 EndAngle=6.28319
    g7: LineSegment StartX=26.25 StartY=-4 StartZ=0 EndX=26.25 EndY=0 EndZ=0
    g8: LineSegment StartX=-18.75 StartY=-14 StartZ=0 EndX=18.75 EndY=-14 EndZ=0
    g9: ArcOfCircle CenterX=-18.75 CenterY=-4 CenterZ=0 NormalX=0 NormalY=0 NormalZ=1 AngleXU=0 Radius=10 StartAngle=3.14159 EndAngle=4.71239
    g10: LineSegment StartX=-28.75 StartY=-4 StartZ=0 EndX=-28.75 EndY=4 EndZ=0
    g11: ArcOfCircle CenterX=-18.75 CenterY=4 CenterZ=0 NormalX=0 NormalY=0 NormalZ=1 AngleXU=0 Radius=10 StartAngle=1.5708 EndAngle=3.14159
    g12: LineSegment StartX=-18.75 StartY=14 StartZ=0 EndX=18.75 EndY=14 EndZ=0
    g13: ArcOfCircle CenterX=18.75 CenterY=4 CenterZ=0 NormalX=0 NormalY=0 NormalZ=1 AngleXU=0 Radius=10 StartAngle=0 EndAngle=1.5708
    g14: ArcOfCircle CenterX=18.75 CenterY=-4 CenterZ=0 NormalX=0 NormalY=0 NormalZ=1 AngleXU=0 Radius=10 StartAngle=4.71239 EndAngle=6.28319
    g15: LineSegment StartX=28.75 StartY=4 StartZ=0 EndX=28.75 EndY=-4 EndZ=0
    g16: LineSegment StartX=-18.75 StartY=-14 StartZ=0 EndX=18.75 EndY=-14 EndZ=0
    g17: LineSegment StartX=18.75 StartY=-11.5 StartZ=0 EndX=-18.75 EndY=-11.5 EndZ=0
    g18: LineSegment StartX=-18.75 StartY=11.5 StartZ=0 EndX=18.75 EndY=11.5 EndZ=0
  constraints (1):
    c: Horizontal(g17)
FEATURE [Sketcher::SketchObject] Sketch022
  MapMode = 5
  Placement = pos=(0,0,0) rot=(1,0,0;1.5708rad)
  Support = -> [XZ_Plane018]
  sketch-geometry (15):
    g0: LineSegment StartX=0 StartY=0 StartZ=0 EndX=12.5 EndY=0 EndZ=0
    g1: LineSegment StartX=12.5 StartY=0 StartZ=0 EndX=12.8 EndY=23 EndZ=0
    g2: LineSegment StartX=12.8 StartY=23 StartZ=0 EndX=29 EndY=29 EndZ=0
    g3: LineSegment StartX=29 StartY=29 StartZ=0 EndX=29 EndY=38.5 EndZ=0
    g4: LineSegment StartX=29 StartY=38.5 StartZ=0 EndX=32.5 EndY=38.5 EndZ=0
    g5: LineSegment StartX=32.5 StartY=38.5 StartZ=0 EndX=32.5 EndY=49.5 EndZ=0
    g6: LineSegment StartX=32.5 StartY=49.5 StartZ=0 EndX=29 EndY=49.5 EndZ=0
    g7: LineSegment StartX=29 StartY=49.5 StartZ=0 EndX=29 EndY=59 EndZ=0
    g8: LineSegment StartX=29 StartY=59 StartZ=0 EndX=11 EndY=65 EndZ=0
    g9: LineSegment StartX=11 StartY=65 StartZ=0 EndX=11 EndY=88 EndZ=0
    g10: LineSegment StartX=11 StartY=88 StartZ=0 EndX=0 EndY=88 EndZ=0
    g11: LineSegment StartX=0 StartY=88 StartZ=0 EndX=0 EndY=0 EndZ=0
    g12: GeomPoint X=0 Y=23 Z=0
    g13: GeomPoint X=0 Y=23 Z=0
    g14: GeomPoint X=12.8 Y=23 Z=0
  constraints (39):
    c: Coincident(g0,g-1)
    c: Coincident(g1,g0)
    c: Coincident(g2,g1)
    c: Coincident(g3,g2)
    c: Vertical(g3)
    c: Horizontal(g4)
    c: Coincident(g5,g4)
    c: Vertical(g5)
    c: Horizontal(g6)
    c: Coincident(g7,g6)
    c: Vertical(g7)
    c: Coincident(g9,g8)
    c: Vertical(g9)
    c: Coincident(g10,g9)
    c: Horizontal(g10)
    c: Coincident(g11,g0)
    c: Vertical(g11)
    c: Horizontal(g0)
    c: DistanceX(g0,g0) = 12.5
    c: Coincident(g13,g12)
    c: Coincident(g14,g1)
    c: Horizontal(g12,g1)
    c: DistanceX(g12,g1) = 12.8
    c: DistanceX(g10,g10) = 11
    c: Coincident(g10,g11)
    c: PointOnObject(g12,g11)
    c: DistanceY(g1,g1) = 23
    c: DistanceX(g12,g4) = 32.5
    c: Coincident(g4,g3)
    c: Coincident(g7,g8)
    c: Coincident(g5,g6)
    c: DistanceX(g12,g2) = 29
    c: DistanceY(g2,g7) = 30
    c: DistanceY(g11,g11) = 88
    c: DistanceY(g9,g9) = 23
    c: DistanceY(g5,g5) = 11
    c: Equal(g6,g4)
    c: Equal(g7,g3)
    c: DistanceY(g7,g9) = 29
FEATURE [PartDesign::Revolution] Revolution002
  Angle = 360
  Axis = (0,2e-16,1)
  Base = (0,0,0)
  Placement = pos=(0,0,0) rot=(1,0,0;1.5708rad)
  Profile = -> Sketch022
  ReferenceAxis = -> Sketch022 [V_Axis]
  Reversed = true
FEATURE [PartDesign::Body] Body018  label="Intersurgical"
  Group = -> [Sketch022,Revolution002]
  Origin = -> Origin018
  Placement = pos=(0,28,-140) rot=(1,0,0;0rad)
  Tip = -> Revolution002
FEATURE [PartDesign::Pad] Pad001
  Length = 26
  Length2 = 100
  Profile = -> Sketch001
  Reversed = true
  Type = 0
FEATURE [PartDesign::Body] Body001  label="buffer"
  Group = -> [Sketch001,Pad001]
  Origin = -> Origin001
  Placement = pos=(0,0,4) rot=(0,0,1;0rad)
  Tip = -> Pad001
FEATURE [Sketcher::SketchObject] Sketch023
  MapMode = 5
  Support = -> [XY_Plane019]
  sketch-geometry (19):
    g0: ArcOfCircle CenterX=18.75 CenterY=4 CenterZ=0 NormalX=0 NormalY=0 NormalZ=1 AngleXU=0 Radius=7.5 StartAngle=0 EndAngle=1.57079
    g1: LineSegment StartX=26.25 StartY=4 StartZ=0 EndX=26.25 EndY=0 EndZ=0
    g2: ArcOfCircle CenterX=-18.75 CenterY=4 CenterZ=0 NormalX=0 NormalY=0 NormalZ=1 AngleXU=0 Radius=7.5 StartAngle=1.5708 EndAngle=3.14159
    g3: LineSegment StartX=-26.25 StartY=4 StartZ=0 EndX=-26.25 EndY=0 EndZ=0
    g4: LineSegment StartX=-26.25 StartY=0 StartZ=0 EndX=-26.25 EndY=-4 EndZ=0
    g5: ArcOfCircle CenterX=-18.75 CenterY=-4 CenterZ=0 NormalX=0 NormalY=0 NormalZ=1 AngleXU=0 Radius=7.5 StartAngle=3.14159 EndAngle=4.71239
    g6: ArcOfCircle CenterX=18.75 CenterY=-4 CenterZ=0 NormalX=0 NormalY=0 NormalZ=1 AngleXU=0 Radius=7.5 StartAngle=4.71239 EndAngle=6.28319
    g7: LineSegment StartX=26.25 StartY=-4 StartZ=0 EndX=26.25 EndY=0 EndZ=0
    g8: LineSegment StartX=-18.75 StartY=-14 StartZ=0 EndX=18.75 EndY=-14 EndZ=0
    g9: ArcOfCircle CenterX=-18.75 CenterY=-4 CenterZ=0 NormalX=0 NormalY=0 NormalZ=1 AngleXU=0 Radius=10 StartAngle=3.14159 EndAngle=4.71239
    g10: LineSegment StartX=-28.75 StartY=-4 StartZ=0 EndX=-28.75 EndY=4 EndZ=0
    g11: ArcOfCircle CenterX=-18.75 CenterY=4 CenterZ=0 NormalX=0 NormalY=0 NormalZ=1 AngleXU=0 Radius=10 StartAngle=1.5708 EndAngle=3.14159
    g12: LineSegment StartX=-18.75 StartY=14 StartZ=0 EndX=18.75 EndY=14 EndZ=0
    g13: ArcOfCircle CenterX=18.75 CenterY=4 CenterZ=0 NormalX=0 NormalY=0 NormalZ=1 AngleXU=0 Radius=10 StartAngle=0 EndAngle=1.5708
    g14: ArcOfCircle CenterX=18.75 CenterY=-4 CenterZ=0 NormalX=0 NormalY=0 NormalZ=1 AngleXU=0 Radius=10 StartAngle=4.71239 EndAngle=6.28319
    g15: LineSegment StartX=28.75 StartY=4 StartZ=0 EndX=28.75 EndY=-4 EndZ=0
    g16: LineSegment StartX=-18.75 StartY=-14 StartZ=0 EndX=18.75 EndY=-14 EndZ=0
    g17: LineSegment StartX=18.75 StartY=-11.5 StartZ=0 EndX=-18.75 EndY=-11.5 EndZ=0
    g18: LineSegment StartX=-18.75 StartY=11.5 StartZ=0 EndX=18.75 EndY=11.5 EndZ=0
  constraints (55):
    c: Coincident(g1,g0)
    c: Vertical(g1)
    c: Coincident(g3,g2)
    c: PointOnObject(g3,g-1)
    c: Vertical(g3)
    c: Coincident(g4,g3)
    c: Vertical(g4)
    c: Coincident(g5,g4)
    c: Coincident(g7,g6)
    c: Coincident(g7,g1)
    c: Vertical(g7)
    c: Equal(g7,g1)
    c: Equal(g1,g3)
    c: Equal(g3,g4)
    c: DistanceX(g3,g1) = 52.5
    c: Symmetric(g2,g5,g-1)
    c: Symmetric(g0,g6,g-1)
    c: Symmetric(g2,g0,g-2)
    c: DistanceY(g6,g0) = 8
    c: Radius(g0) = 7.5
    c: Horizontal(g0,g0)
    c: Vertical(g5,g8)
    c: Coincident(g9,g5)
    c: Coincident(g9,g8)
    c: Coincident(g10,g9)
    c: Vertical(g10)
    c: Coincident(g11,g2)
    c: Coincident(g11,g10)
    c: Coincident(g12,g11)
    c: Coincident(g13,g0)
    c: Vertical(g8,g6)
    c: Coincident(g14,g6)
    c: Coincident(g14,g8)
    c: Coincident(g15,g13)
    c: Coincident(g15,g14)
    c: DistanceY(g8,g5) = 2.5
    c: Horizontal(g4,g9)
    c: Horizontal(g10,g2)
    c: Vertical(g13,g14)
    c: Horizontal(g0,g13)
    c: Vertical(g13,g0)
    c: Horizontal(g12)
    c: Horizontal(g14,g6)
    c: Coincident(g12,g13)
    c: Vertical(g2,g11)
    c: Vertical(g2,g5)
    c: Symmetric(g2,g0,g-2)
    c: Symmetric(g2,g0,g-2)
    c: Coincident(g16,g8)
    c: Coincident(g16,g8)
    c: Horizontal(g16)
    c: Coincident(g17,g6)
    c: Coincident(g17,g5)
    c: Coincident(g18,g2)
    c: Coincident(g18,g0)
FEATURE [PartDesign::Pad] Pad013
  Length = 14
  Length2 = 100
  Profile = -> Sketch023
  Type = 0
FEATURE [PartDesign::Body] Body019  label="transition-shared001"
  Group = -> [Sketch023,Pad013]
  Origin = -> Origin019
  Placement = pos=(0,0,-34) rot=(-1,0,0;1.5708rad)
  Tip = -> Pad013
FEATURE [Part::Cut] Cut
  Base = -> Body019
  Tool = -> Body010
FEATURE [Part::Cut] Cut005
  Base = -> Cut
  Tool = -> Body009
FEATURE [Part::MultiFuse] Fusion001
  Shapes = -> [Body008,Cut003,Cut004,Body001]
FEATURE [Part::MultiFuse] Fusion
  Shapes = -> [Fusion001,Cut005]
FEATURE [Part::MultiFuse] Fusion002
  Shapes = -> [Fusion,Body]
FEATURE [Sketcher::SketchObject] Sketch024
  MapMode = 5
  Support = -> [XY_Plane015]
  sketch-geometry (1):
    g0: LineSegment StartX=-30.5 StartY=-14.5 StartZ=0 EndX=32.3316 EndY=-14.5 EndZ=0
  constraints (1):
    c: Horizontal(g0)
FEATURE [PartDesign::Revolution] Revolution
  Angle = 90
  Axis = (1,0,0)
  Base = (-30.5,-14.5,0)
  Profile = -> Sketch020
  ReferenceAxis = -> Sketch024 [Edge1]
FEATURE [PartDesign::Body] Body015  label="transition-shared"
  Group = -> [Sketch020,Sketch024,Revolution]
  Origin = -> Origin015
  Placement = pos=(0,28,-48) rot=(-1,0,0;0rad)
  Tip = -> Revolution
FEATURE [Part::MultiFuse] Fusion003
  Placement = pos=(0,0,-0.5) rot=(0,0,1;0rad)
  Shapes = -> [Body015,Body006]
FEATURE [Part::MultiFuse] Fusion004
  Shapes = -> [Fusion002,Fusion003]
FEATURE [Mesh::Feature] Mesh  label="Fusion004 (Meshed)"
